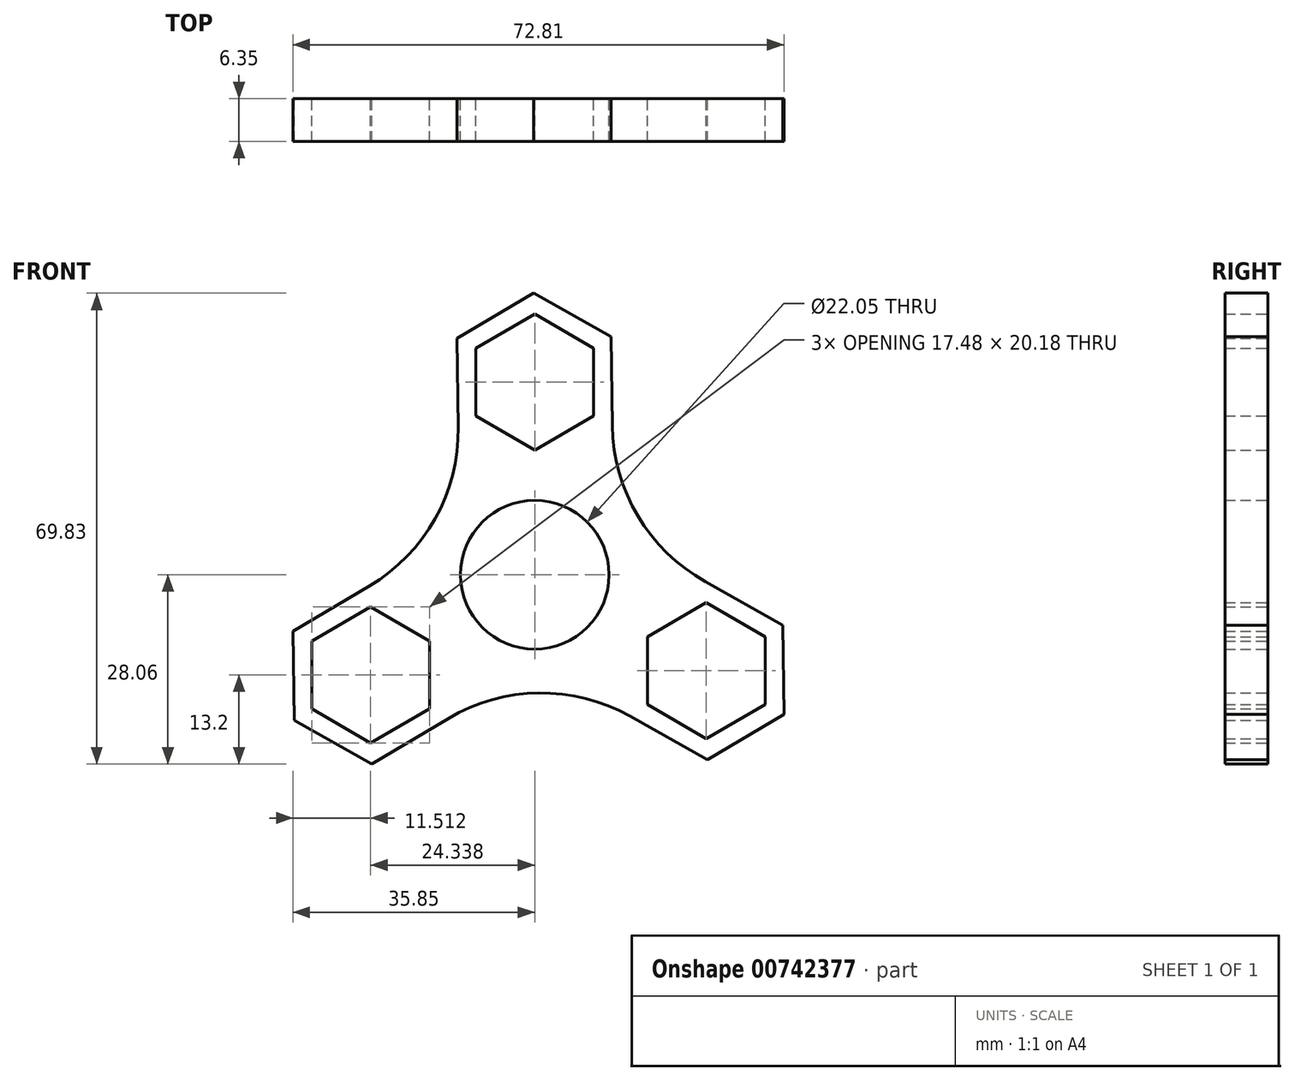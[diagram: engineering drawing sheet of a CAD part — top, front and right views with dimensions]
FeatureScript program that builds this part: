
annotation { "Feature Type Name" : "Feature", "Feature Type Description" : "" }
export const myFeature = defineFeature(function(context is Context, id is Id, definition is map)
    precondition{}
    {
        {
            var Q0;
            Q0=qCreatedBy(makeId("Front.planeOp"),FACE);
            var sketch = newSketch(context, id + "F0", { "sketchPlane" : qUnion([Q0])});
            skCircle(sketch, "E0", {"center": v(0, 0) * mm, "radius": 11.02 * mm});
            skCircle(sketch, "E1", {"center": v(0, 0) * mm, "radius": 14.29 * mm});
            skCircle(sketch, "E2.cCircle", {"center": v(0, 28.58) * mm, "radius": 11.43 * mm, "construction": true});
            skLineSegment(sketch, "E2.0", {"start": v(11.51, 22.12) * mm, "end": v(0.17, 15.38) * mm});
            skLineSegment(sketch, "E2.1", {"start": v(0.17, 15.38) * mm, "end": v(-11.34, 21.83) * mm});
            skLineSegment(sketch, "E2.2", {"start": v(-11.34, 21.83) * mm, "end": v(-11.51, 35.03) * mm});
            skLineSegment(sketch, "E2.3", {"start": v(-11.51, 35.03) * mm, "end": v(-0.17, 41.77) * mm});
            skLineSegment(sketch, "E2.4", {"start": v(-0.17, 41.77) * mm, "end": v(11.34, 35.32) * mm});
            skLineSegment(sketch, "E2.5", {"start": v(11.34, 35.32) * mm, "end": v(11.51, 22.12) * mm});
            skPoint(sketch, "E2.0.midPoint", {"position": v(5.84, 18.75) * mm});
            skCircle(sketch, "E3.cCircle", {"center": v(0, 28.58) * mm, "radius": 8.74 * mm, "construction": true});
            skLineSegment(sketch, "E3.0", {"start": v(8.74, 33.62) * mm, "end": v(8.74, 23.53) * mm});
            skLineSegment(sketch, "E3.1", {"start": v(8.74, 23.53) * mm, "end": v(0, 18.49) * mm});
            skLineSegment(sketch, "E3.2", {"start": v(0, 18.49) * mm, "end": v(-8.74, 23.53) * mm});
            skLineSegment(sketch, "E3.3", {"start": v(-8.74, 23.53) * mm, "end": v(-8.74, 33.62) * mm});
            skLineSegment(sketch, "E3.4", {"start": v(-8.74, 33.62) * mm, "end": v(0, 38.66) * mm});
            skLineSegment(sketch, "E3.5", {"start": v(0, 38.66) * mm, "end": v(8.74, 33.62) * mm});
            skPoint(sketch, "E3.0.midPoint", {"position": v(8.74, 28.58) * mm});
            skLineSegment(sketch, "E4.1.0", {"start": v(-12.82, -21.31) * mm, "end": v(-24.17, -28.06) * mm});
            skLineSegment(sketch, "E4.1.1", {"start": v(-24.5, -1.66) * mm, "end": v(-13, -8.11) * mm});
            skLineSegment(sketch, "E4.1.2", {"start": v(-13, -8.11) * mm, "end": v(-12.82, -21.31) * mm});
            skLineSegment(sketch, "E4.1.3", {"start": v(-24.17, -28.06) * mm, "end": v(-35.68, -21.6) * mm});
            skLineSegment(sketch, "E4.1.4", {"start": v(-35.68, -21.6) * mm, "end": v(-35.85, -8.4) * mm});
            skLineSegment(sketch, "E4.1.5", {"start": v(-24.34, -24.95) * mm, "end": v(-33.08, -19.9) * mm});
            skCircle(sketch, "E4.1.6", {"center": v(-24.34, -14.86) * mm, "radius": 11.43 * mm, "construction": true});
            skPoint(sketch, "E4.1.7", {"position": v(-28.7, -7.3) * mm});
            skLineSegment(sketch, "E4.1.8", {"start": v(-35.85, -8.4) * mm, "end": v(-24.5, -1.66) * mm});
            skCircle(sketch, "E4.1.9", {"center": v(-24.34, -14.86) * mm, "radius": 8.74 * mm, "construction": true});
            skPoint(sketch, "E4.1.10", {"position": v(-18.75, -4.89) * mm});
            skLineSegment(sketch, "E4.1.11", {"start": v(-15.6, -9.82) * mm, "end": v(-15.6, -19.9) * mm});
            skLineSegment(sketch, "E4.1.12", {"start": v(-15.6, -19.9) * mm, "end": v(-24.34, -24.95) * mm});
            skLineSegment(sketch, "E4.1.13", {"start": v(-33.08, -19.9) * mm, "end": v(-33.08, -9.82) * mm});
            skLineSegment(sketch, "E4.1.14", {"start": v(-33.08, -9.82) * mm, "end": v(-24.34, -4.77) * mm});
            skLineSegment(sketch, "E4.1.15", {"start": v(-24.34, -4.77) * mm, "end": v(-15.6, -9.82) * mm});
            skLineSegment(sketch, "E4.2.0", {"start": v(25.28, -1.02) * mm, "end": v(36.8, -7.47) * mm});
            skLineSegment(sketch, "E4.2.1", {"start": v(14.1, -20.97) * mm, "end": v(13.93, -7.77) * mm});
            skLineSegment(sketch, "E4.2.2", {"start": v(13.93, -7.77) * mm, "end": v(25.28, -1.02) * mm});
            skLineSegment(sketch, "E4.2.3", {"start": v(36.8, -7.47) * mm, "end": v(36.96, -20.67) * mm});
            skLineSegment(sketch, "E4.2.4", {"start": v(36.96, -20.67) * mm, "end": v(25.62, -27.42) * mm});
            skLineSegment(sketch, "E4.2.5", {"start": v(34.18, -9.18) * mm, "end": v(34.18, -19.26) * mm});
            skCircle(sketch, "E4.2.6", {"center": v(25.45, -14.22) * mm, "radius": 11.43 * mm, "construction": true});
            skPoint(sketch, "E4.2.7", {"position": v(21.08, -21.79) * mm});
            skLineSegment(sketch, "E4.2.8", {"start": v(25.62, -27.42) * mm, "end": v(14.1, -20.97) * mm});
            skCircle(sketch, "E4.2.9", {"center": v(25.45, -14.22) * mm, "radius": 8.74 * mm, "construction": true});
            skPoint(sketch, "E4.2.10", {"position": v(14.02, -14.37) * mm});
            skLineSegment(sketch, "E4.2.11", {"start": v(16.7, -9.18) * mm, "end": v(25.45, -4.13) * mm});
            skLineSegment(sketch, "E4.2.12", {"start": v(25.45, -4.13) * mm, "end": v(34.18, -9.18) * mm});
            skLineSegment(sketch, "E4.2.13", {"start": v(34.18, -19.26) * mm, "end": v(25.45, -24.3) * mm});
            skLineSegment(sketch, "E4.2.14", {"start": v(25.45, -24.3) * mm, "end": v(16.7, -19.26) * mm});
            skLineSegment(sketch, "E4.2.15", {"start": v(16.7, -19.26) * mm, "end": v(16.7, -9.18) * mm});
            skPoint(sketch, "E4.center", {"position": v(0.37, -0.17) * mm});
            skArc(sketch, "E5", {"start": v(-24.5, -1.66) * mm, "mid": v(-14.78, 8.32) * mm, "end": v(-11.34, 21.83) * mm});
            skArc(sketch, "E6", {"start": v(14.1, -20.97) * mm, "mid": v(0.6, -17.53) * mm, "end": v(-12.82, -21.31) * mm});
            skPoint(sketch, "E7.start.orphan", {"position": v(11.51, 21.83) * mm});
            skArc(sketch, "E8", {"start": v(11.51, 22.12) * mm, "mid": v(15.3, 8.7) * mm, "end": v(25.28, -1.02) * mm});
            skSolve(sketch);
        }
        {
            var Q0;
            Q0 = qSketchRegion(id + "F0", true);
            var Q1;
            Q1=makeQuery(id+"F0.imprint","IMPRINT",FACE,{"disambiguationData":[TD([[makeQuery(id+"F0.imprint","IMPRINT",EDGE,{"derivedFrom":sQuery(id+"F0.wireOp",EDGE,"E0")}),-1.0]])]});
            extrude(context, id + "F1", {"entities" : qUnion([Q0, Q1]), "depth" : 6.35 * mm, "offsetDistance" : 25.4 * mm});
        }
    });
